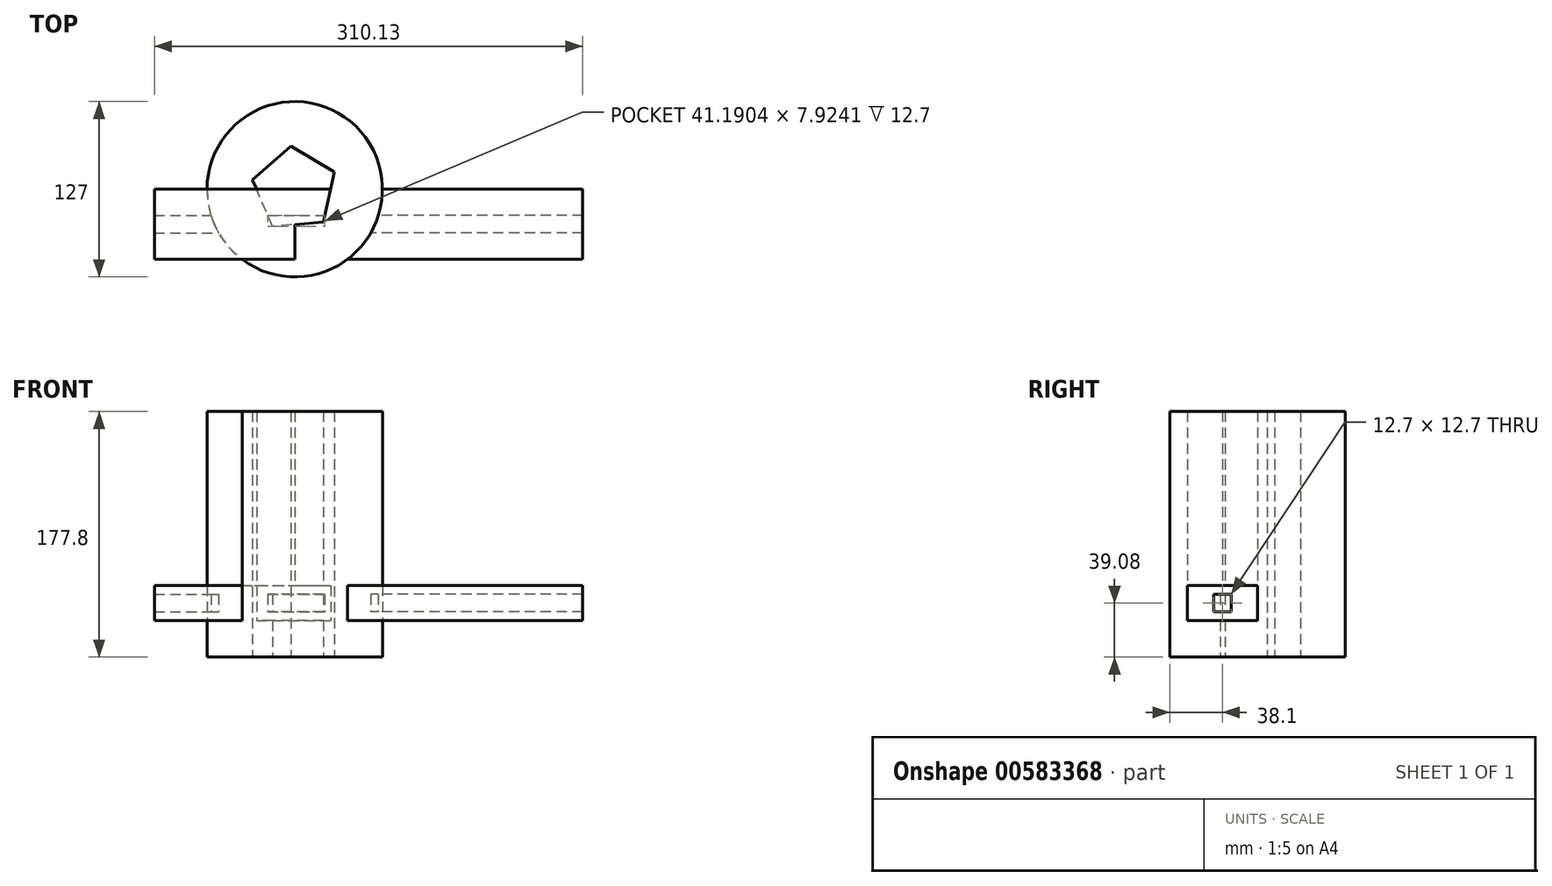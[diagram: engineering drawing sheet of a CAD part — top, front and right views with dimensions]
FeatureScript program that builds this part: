
annotation { "Feature Type Name" : "Feature", "Feature Type Description" : "" }
export const myFeature = defineFeature(function(context is Context, id is Id, definition is map)
    precondition{}
    {
        {
            var Q0;
            Q0=qCreatedBy(makeId("Top.planeOp"),FACE);
            var sketch = newSketch(context, id + "F0", { "sketchPlane" : qUnion([Q0])});
            skCircle(sketch, "E0", {"center": v(0, 0) * mm, "radius": 63.5 * mm});
            skCircle(sketch, "E1.cCircle", {"center": v(0, 0) * mm, "radius": 25.4 * mm, "construction": true});
            skLineSegment(sketch, "E1.0", {"start": v(-30.62, 6.94) * mm, "end": v(-2.86, 31.27) * mm});
            skLineSegment(sketch, "E1.1", {"start": v(-2.86, 31.27) * mm, "end": v(28.85, 12.38) * mm});
            skLineSegment(sketch, "E1.2", {"start": v(28.85, 12.38) * mm, "end": v(20.69, -23.62) * mm});
            skLineSegment(sketch, "E1.3", {"start": v(20.69, -23.62) * mm, "end": v(-16.07, -26.97) * mm});
            skLineSegment(sketch, "E1.4", {"start": v(-16.07, -26.97) * mm, "end": v(-30.62, 6.94) * mm});
            skPoint(sketch, "E1.0.midPoint", {"position": v(-16.74, 19.1) * mm});
            skSolve(sketch);
        }
        {
            var Q0;
            Q0 = qSketchRegion(id + "F0", true);
            extrude(context, id + "F1", {"entities" : qUnion([Q0]), "depth" : 50.8 * mm, "offsetDistance" : 25.4 * mm});
        }
        {
            var Q0;
            Q0=qCreatedBy(makeId("Right.planeOp"),FACE);
            var sketch = newSketch(context, id + "F2", { "sketchPlane" : qUnion([Q0])});
            skLineSegment(sketch, "E2.bottom", {"start": v(0, 26.38) * mm, "end": v(-50.8, 26.38) * mm});
            skLineSegment(sketch, "E2.top", {"start": v(0, 51.78) * mm, "end": v(-50.8, 51.78) * mm});
            skLineSegment(sketch, "E2.left", {"start": v(0, 26.38) * mm, "end": v(0, 51.78) * mm});
            skLineSegment(sketch, "E2.right", {"start": v(-50.8, 26.38) * mm, "end": v(-50.8, 51.78) * mm});
            skPoint(sketch, "E2.middle", {"position": v(-25.4, 39.08) * mm});
            skLineSegment(sketch, "E3.bottom", {"start": v(-19.05, 32.73) * mm, "end": v(-31.75, 32.73) * mm});
            skLineSegment(sketch, "E3.top", {"start": v(-19.05, 45.43) * mm, "end": v(-31.75, 45.43) * mm});
            skLineSegment(sketch, "E3.left", {"start": v(-19.05, 32.73) * mm, "end": v(-19.05, 45.43) * mm});
            skLineSegment(sketch, "E3.right", {"start": v(-31.75, 32.73) * mm, "end": v(-31.75, 45.43) * mm});
            skSolve(sketch);
        }
        {
            var Q0;
            Q0 = qSketchRegion(id + "F2", true);
            extrude(context, id + "F3", {"entities" : qUnion([Q0]), "operationType" : NewBodyOperationType.ADD, "oppositeDirection" : true, "depth" : 101.6 * mm, "offsetDistance" : 25.4 * mm});
        }
        {
            var Q0;
            Q0=makeQuery(id+"F1.opExtrude","CAP_FACE",FACE,{"disambiguationData":[OSD([sQuery(id+"F0.wireOp",EDGE,"E0"),sQuery(id+"F0.wireOp",EDGE,"E1.0"),sQuery(id+"F0.wireOp",EDGE,"E1.1"),sQuery(id+"F0.wireOp",EDGE,"E1.2"),sQuery(id+"F0.wireOp",EDGE,"E1.3"),sQuery(id+"F0.wireOp",EDGE,"E1.4")])],"isStart":false});
            var sketch = newSketch(context, id + "F4", { "sketchPlane" : qUnion([Q0])});
            skSolve(sketch);
        }
        {
            var Q0;
            Q0 = qSketchRegion(id + "F2", true);
            var Q1;
            Q1 = qSketchRegion(id + "F4", true);
            extrude(context, id + "F5", {"entities" : qUnion([Q0, Q1]), "operationType" : NewBodyOperationType.ADD, "depth" : 208.53 * mm, "offsetDistance" : 25.4 * mm});
        }
        {
            var Q0;
            {var subQ3=sQuery(id+"F0.wireOp",EDGE,"E1.0");Q0=makeQuery(id+"F4.imprint","IMPRINT",FACE,{"disambiguationData":[TD([[makeQuery(id+"F4.imprint","IMPRINT",EDGE,{"derivedFrom":makeQuery(id+"F1.opExtrude","CAP_EDGE",EDGE,{"disambiguationData":[OSD([subQ3])],"isStart":false})}),1.0]])]});}
            extrude(context, id + "F6", {"entities" : qUnion([Q0]), "operationType" : NewBodyOperationType.ADD, "depth" : 127 * mm, "offsetDistance" : 25.4 * mm});
        }
    });
